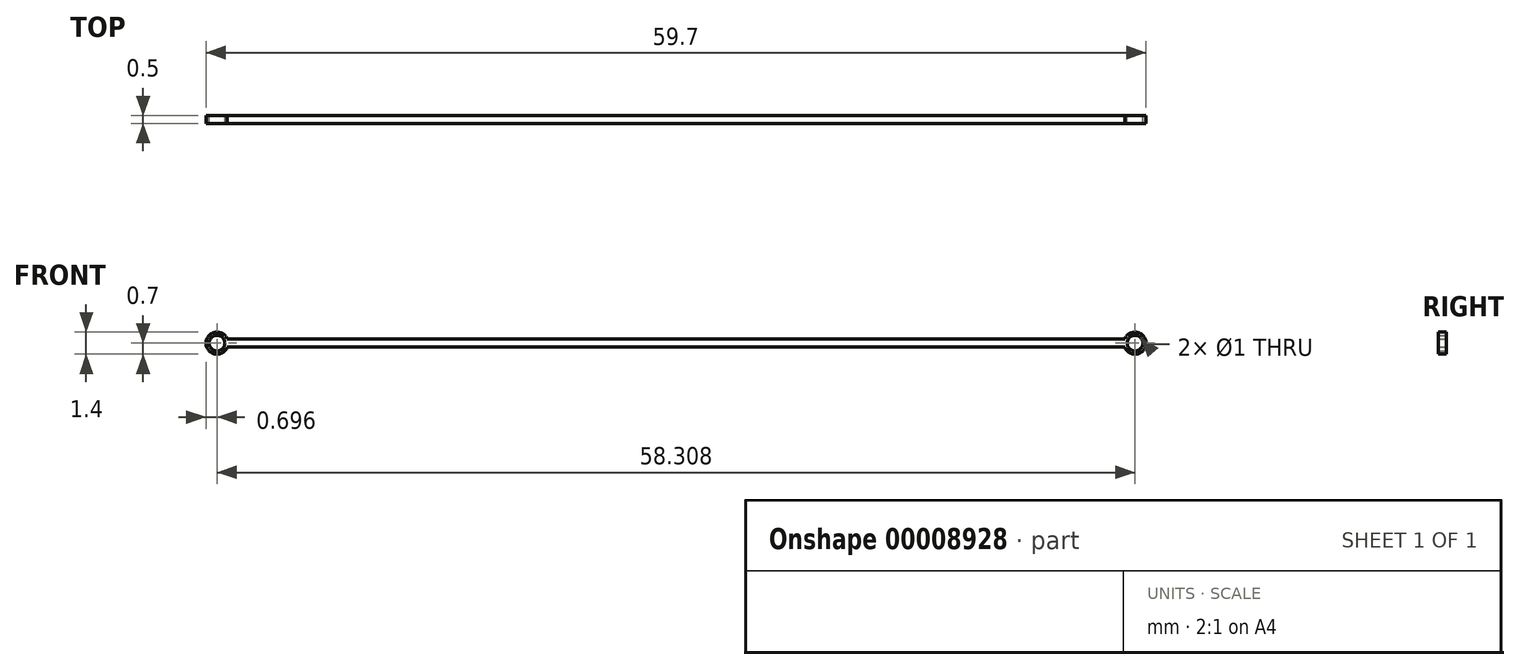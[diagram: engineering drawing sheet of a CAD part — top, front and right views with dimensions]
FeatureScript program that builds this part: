
annotation { "Feature Type Name" : "Feature", "Feature Type Description" : "" }
export const myFeature = defineFeature(function(context is Context, id is Id, definition is map)
    precondition{}
    {
        {
            var Q0;
            Q0=qCreatedBy(makeId("Front.planeOp"),FACE);
            var sketch = newSketch(context, id + "F0", { "sketchPlane" : qUnion([Q0])});
            skLineSegment(sketch, "E0.bottom", {"start": v(0, 0) * mm, "end": v(57, 0) * mm});
            skLineSegment(sketch, "E0.top", {"start": v(0, 0.5) * mm, "end": v(57, 0.5) * mm});
            skLineSegment(sketch, "E0.left", {"start": v(0, 0) * mm, "end": v(0, 0.5) * mm});
            skLineSegment(sketch, "E0.right", {"start": v(57, 0) * mm, "end": v(57, 0.5) * mm});
            skArc(sketch, "E1", {"start": v(0, 0.5) * mm, "mid": v(-1.35, 0.25) * mm, "end": v(0, 0) * mm});
            skArc(sketch, "E2", {"start": v(57, 0) * mm, "mid": v(58.35, 0.25) * mm, "end": v(57, 0.5) * mm});
            skCircle(sketch, "E3", {"center": v(-0.65, 0.25) * mm, "radius": 0.5 * mm});
            skCircle(sketch, "E4", {"center": v(57.65, 0.25) * mm, "radius": 0.5 * mm});
            skSolve(sketch);
        }
        {
            var Q0;
            Q0 = qSketchRegion(id + "F0", true);
            extrude(context, id + "F1", {"entities" : qUnion([Q0]), "depth" : 0.5 * mm});
        }
    });
